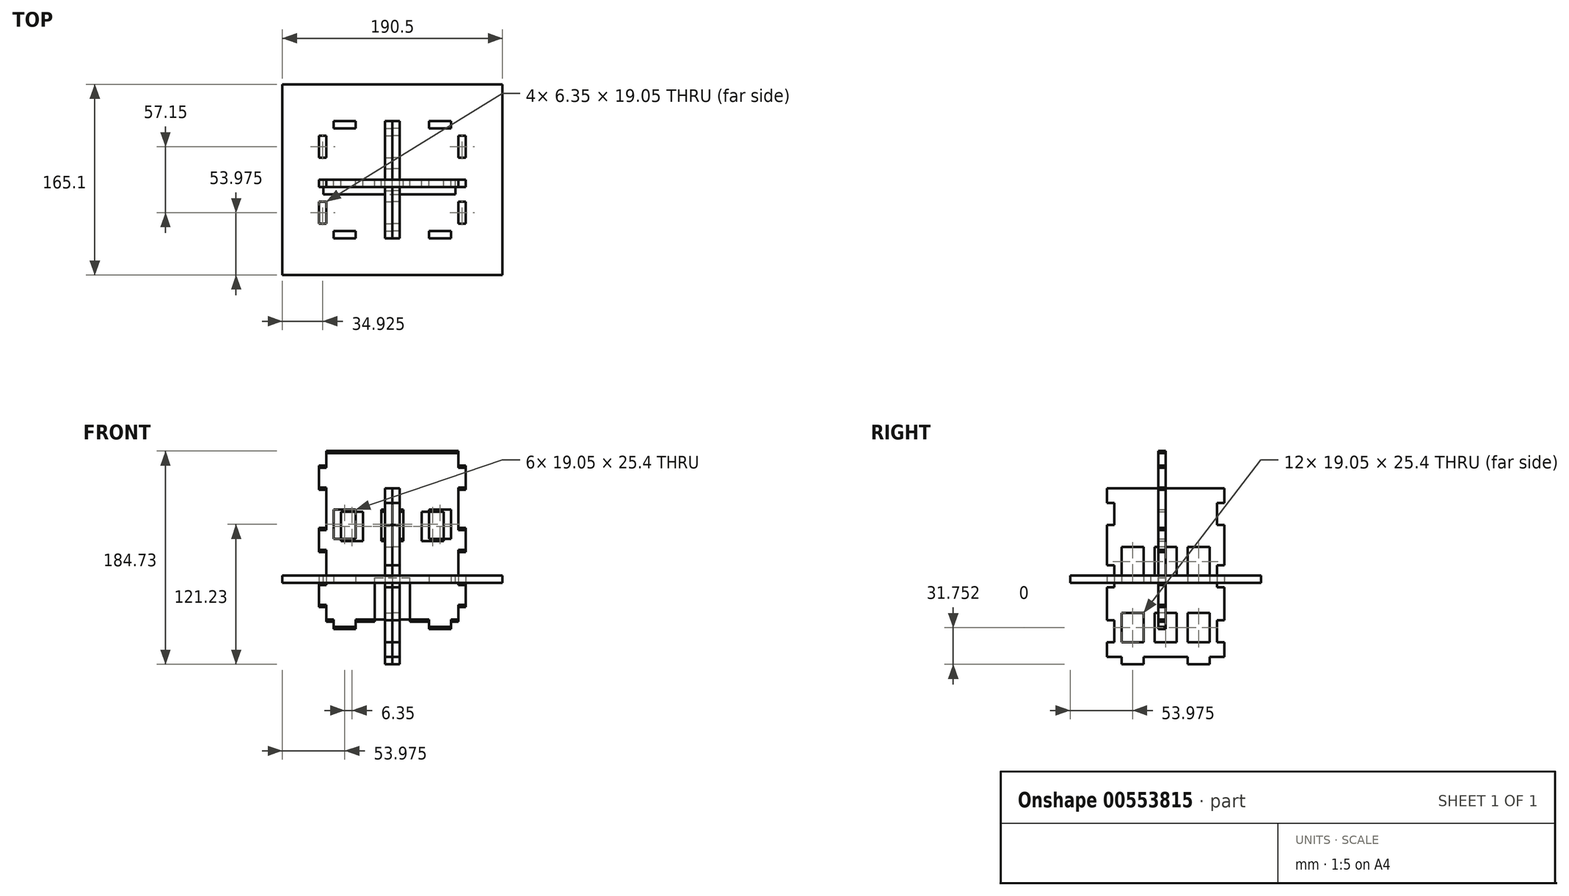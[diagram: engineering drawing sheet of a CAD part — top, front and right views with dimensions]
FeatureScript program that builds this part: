
annotation { "Feature Type Name" : "Feature", "Feature Type Description" : "" }
export const myFeature = defineFeature(function(context is Context, id is Id, definition is map)
    precondition{}
    {
        {
            var Q0;
            Q0=qCreatedBy(makeId("Top.planeOp"),FACE);
            var sketch = newSketch(context, id + "F0", { "sketchPlane" : qUnion([Q0])});
            skLineSegment(sketch, "E0.bottom", {"start": v(63.5, 50.8) * mm, "end": v(-63.5, 50.8) * mm});
            skLineSegment(sketch, "E0.top", {"start": v(63.5, -50.8) * mm, "end": v(-63.5, -50.8) * mm});
            skLineSegment(sketch, "E0.left", {"start": v(63.5, 50.8) * mm, "end": v(63.5, -50.8) * mm});
            skLineSegment(sketch, "E0.right", {"start": v(-63.5, 50.8) * mm, "end": v(-63.5, -50.8) * mm});
            skPoint(sketch, "E0.middle", {"position": v(0, 0) * mm});
            skLineSegment(sketch, "E1", {"start": v(-63.5, -44.45) * mm, "end": v(63.5, -44.45) * mm});
            skLineSegment(sketch, "E2", {"start": v(-50.8, -44.45) * mm, "end": v(-50.8, -50.8) * mm});
            skLineSegment(sketch, "E3", {"start": v(-31.75, -44.45) * mm, "end": v(-31.75, -50.8) * mm});
            skLineSegment(sketch, "E4", {"start": v(50.8, -44.45) * mm, "end": v(50.8, -50.8) * mm});
            skLineSegment(sketch, "E5", {"start": v(31.75, -44.45) * mm, "end": v(31.75, -50.8) * mm});
            skLineSegment(sketch, "E6.MirrorCS", {"start": v(-63.5, 44.45) * mm, "end": v(63.5, 44.45) * mm});
            skLineSegment(sketch, "E7.MirrorCS", {"start": v(50.8, 44.45) * mm, "end": v(50.8, 50.8) * mm});
            skLineSegment(sketch, "E8.MirrorCS", {"start": v(31.75, 44.45) * mm, "end": v(31.75, 50.8) * mm});
            skLineSegment(sketch, "E9.MirrorCS", {"start": v(-50.8, 44.45) * mm, "end": v(-50.8, 50.8) * mm});
            skLineSegment(sketch, "E10.MirrorCS", {"start": v(-31.75, 44.45) * mm, "end": v(-31.75, 50.8) * mm});
            skLineSegment(sketch, "E11", {"start": v(57.15, -44.45) * mm, "end": v(57.15, 44.45) * mm});
            skLineSegment(sketch, "E12", {"start": v(57.15, -38.1) * mm, "end": v(63.5, -38.1) * mm});
            skLineSegment(sketch, "E13", {"start": v(57.15, -19.05) * mm, "end": v(63.5, -19.05) * mm});
            skLineSegment(sketch, "E14", {"start": v(57.15, 19.05) * mm, "end": v(63.5, 19.05) * mm});
            skLineSegment(sketch, "E15", {"start": v(57.15, 38.1) * mm, "end": v(63.5, 38.1) * mm});
            skLineSegment(sketch, "E16.MirrorCS", {"start": v(-57.15, -44.45) * mm, "end": v(-57.15, 44.45) * mm});
            skLineSegment(sketch, "E17.MirrorCS", {"start": v(-57.15, 19.05) * mm, "end": v(-63.5, 19.05) * mm});
            skLineSegment(sketch, "E18.MirrorCS", {"start": v(-57.15, 38.1) * mm, "end": v(-63.5, 38.1) * mm});
            skLineSegment(sketch, "E19.MirrorCS", {"start": v(-57.15, -19.05) * mm, "end": v(-63.5, -19.05) * mm});
            skLineSegment(sketch, "E20.MirrorCS", {"start": v(-57.15, -38.1) * mm, "end": v(-63.5, -38.1) * mm});
            skLineSegment(sketch, "E21.bottom", {"start": v(95.25, -82.55) * mm, "end": v(-95.25, -82.55) * mm});
            skLineSegment(sketch, "E21.top", {"start": v(95.25, 82.55) * mm, "end": v(-95.25, 82.55) * mm});
            skLineSegment(sketch, "E21.left", {"start": v(95.25, -82.55) * mm, "end": v(95.25, 82.55) * mm});
            skLineSegment(sketch, "E21.right", {"start": v(-95.25, -82.55) * mm, "end": v(-95.25, 82.55) * mm});
            skSolve(sketch);
        }
        {
            var Q0;
            {var subQ3=sQuery(id+"F0.wireOp",EDGE,"E7.MirrorCS");Q0=makeQuery(id+"F0.imprint","IMPRINT",FACE,{"disambiguationData":[TD([[makeQuery(id+"F0.imprint","IMPRINT",EDGE,{"derivedFrom":subQ3}),-1.0]])]});}
            var Q1;
            {var subQ3=sQuery(id+"F0.wireOp",EDGE,"E9.MirrorCS");Q1=makeQuery(id+"F0.imprint","IMPRINT",FACE,{"disambiguationData":[TD([[makeQuery(id+"F0.imprint","IMPRINT",EDGE,{"derivedFrom":subQ3}),1.0]])]});}
            var Q2;
            {var subQ0=sQuery(id+"F0.wireOp",EDGE,"E8.MirrorCS");Q2=makeQuery(id+"F0.imprint","IMPRINT",FACE,{"disambiguationData":[TD([[makeQuery(id+"F0.imprint","IMPRINT",EDGE,{"derivedFrom":subQ0}),1.0]])]});}
            var Q3;
            {var subQ3=sQuery(id+"F0.wireOp",EDGE,"E2");Q3=makeQuery(id+"F0.imprint","IMPRINT",FACE,{"disambiguationData":[TD([[makeQuery(id+"F0.imprint","IMPRINT",EDGE,{"derivedFrom":subQ3}),-1.0]])]});}
            var Q4;
            {var subQ0=sQuery(id+"F0.wireOp",EDGE,"E3");Q4=makeQuery(id+"F0.imprint","IMPRINT",FACE,{"disambiguationData":[TD([[makeQuery(id+"F0.imprint","IMPRINT",EDGE,{"derivedFrom":subQ0}),1.0]])]});}
            var Q5;
            {var subQ3=sQuery(id+"F0.wireOp",EDGE,"E4");Q5=makeQuery(id+"F0.imprint","IMPRINT",FACE,{"disambiguationData":[TD([[makeQuery(id+"F0.imprint","IMPRINT",EDGE,{"derivedFrom":subQ3}),1.0]])]});}
            var Q6;
            {var subQ3=sQuery(id+"F0.wireOp",EDGE,"E1");var subQ4=sQuery(id+"F0.wireOp",EDGE,"E0.left");var subQ5=makeQuery(id+"F0.imprint","INTERSECT",VERTEX,{"derivedFrom":[subQ4,subQ3]});Q6=makeQuery(id+"F0.imprint","IMPRINT",FACE,{"disambiguationData":[TD([[makeQuery(id+"F0.imprint","IMPRINT",EDGE,{"disambiguationData":[TD([[subQ5,1.0]])],"derivedFrom":subQ4}),-1.0]])]});}
            var Q7;
            {var subQ4=sQuery(id+"F0.wireOp",EDGE,"E1");var subQ11=makeQuery(id+"F0.imprint","INTERSECT",VERTEX,{"derivedFrom":[subQ4,sQuery(id+"F0.wireOp",EDGE,"E2")]});Q7=makeQuery(id+"F0.imprint","IMPRINT",FACE,{"disambiguationData":[TD([[makeQuery(id+"F0.imprint","IMPRINT",EDGE,{"disambiguationData":[TD([[subQ11,1.0]])],"derivedFrom":subQ4}),1.0]])]});}
            var Q8;
            {var subQ0=sQuery(id+"F0.wireOp",EDGE,"E13");Q8=makeQuery(id+"F0.imprint","IMPRINT",FACE,{"disambiguationData":[TD([[makeQuery(id+"F0.imprint","IMPRINT",EDGE,{"derivedFrom":subQ0}),1.0]])]});}
            var Q9;
            {var subQ3=sQuery(id+"F0.wireOp",EDGE,"E15");Q9=makeQuery(id+"F0.imprint","IMPRINT",FACE,{"disambiguationData":[TD([[makeQuery(id+"F0.imprint","IMPRINT",EDGE,{"derivedFrom":subQ3}),1.0]])]});}
            var Q10;
            {var subQ3=sQuery(id+"F0.wireOp",EDGE,"E20.MirrorCS");Q10=makeQuery(id+"F0.imprint","IMPRINT",FACE,{"disambiguationData":[TD([[makeQuery(id+"F0.imprint","IMPRINT",EDGE,{"derivedFrom":subQ3}),1.0]])]});}
            var Q11;
            {var subQ3=sQuery(id+"F0.wireOp",EDGE,"E18.MirrorCS");Q11=makeQuery(id+"F0.imprint","IMPRINT",FACE,{"disambiguationData":[TD([[makeQuery(id+"F0.imprint","IMPRINT",EDGE,{"derivedFrom":subQ3}),-1.0]])]});}
            var Q12;
            {var subQ0=sQuery(id+"F0.wireOp",EDGE,"E17.MirrorCS");Q12=makeQuery(id+"F0.imprint","IMPRINT",FACE,{"disambiguationData":[TD([[makeQuery(id+"F0.imprint","IMPRINT",EDGE,{"derivedFrom":subQ0}),1.0]])]});}
            var Q13;
            Q13=makeQuery(id+"F0.imprint","IMPRINT",FACE,{"disambiguationData":[TD([[makeQuery(id+"F0.imprint","IMPRINT",EDGE,{"derivedFrom":sQuery(id+"F0.wireOp",EDGE,"E21.bottom")}),-1.0]])]});
            extrude(context, id + "F1", {"entities" : qUnion([Q0, Q1, Q2, Q3, Q4, Q5, Q6, Q7, Q8, Q9, Q10, Q11, Q12, Q13]), "depth" : 6.35 * mm, "offsetDistance" : 25.4 * mm});
        }
        {
            var Q0;
            Q0=qCreatedBy(makeId("Front.planeOp"),FACE);
            var sketch = newSketch(context, id + "F2", { "sketchPlane" : qUnion([Q0])});
            skLineSegment(sketch, "E22.bottom", {"start": v(-63.5, 112.4) * mm, "end": v(63.5, 112.4) * mm});
            skLineSegment(sketch, "E22.top", {"start": v(-63.5, -40) * mm, "end": v(63.5, -40) * mm});
            skLineSegment(sketch, "E22.left", {"start": v(-63.5, 112.4) * mm, "end": v(-63.5, -40) * mm});
            skLineSegment(sketch, "E22.right", {"start": v(63.5, 112.4) * mm, "end": v(63.5, -40) * mm});
            skPoint(sketch, "E22.middle", {"position": v(0, 36.2) * mm});
            skLineSegment(sketch, "E23", {"start": v(-63.5, -33.66) * mm, "end": v(63.5, -33.66) * mm});
            skLineSegment(sketch, "E24", {"start": v(-50.8, -33.66) * mm, "end": v(-50.8, -40) * mm});
            skLineSegment(sketch, "E25", {"start": v(50.8, -40) * mm, "end": v(50.8, -33.66) * mm});
            skLineSegment(sketch, "E26", {"start": v(-31.75, -40) * mm, "end": v(-31.75, -33.66) * mm});
            skLineSegment(sketch, "E27", {"start": v(31.75, -40) * mm, "end": v(31.75, -33.66) * mm});
            skLineSegment(sketch, "E28.bottom", {"start": v(-15.24, -33.66) * mm, "end": v(15.24, -33.66) * mm});
            skLineSegment(sketch, "E28.top", {"start": v(-15.24, 4.45) * mm, "end": v(15.24, 4.45) * mm});
            skLineSegment(sketch, "E28.left", {"start": v(-15.24, -33.66) * mm, "end": v(-15.24, 4.45) * mm});
            skLineSegment(sketch, "E28.right", {"start": v(15.24, -33.66) * mm, "end": v(15.24, 4.45) * mm});
            skLineSegment(sketch, "E29", {"start": v(-63.5, 17.14) * mm, "end": v(63.5, 17.14) * mm, "construction": true});
            skLineSegment(sketch, "E30", {"start": v(-63.5, 23.5) * mm, "end": v(63.5, 23.5) * mm, "construction": true});
            skLineSegment(sketch, "E31", {"start": v(-63.5, 36.2) * mm, "end": v(63.5, 36.2) * mm, "construction": true});
            skLineSegment(sketch, "E32.bottom", {"start": v(-44.45, 36.2) * mm, "end": v(-25.4, 36.2) * mm});
            skLineSegment(sketch, "E32.top", {"start": v(-44.45, 61.6) * mm, "end": v(-25.4, 61.6) * mm});
            skLineSegment(sketch, "E32.left", {"start": v(-44.45, 36.2) * mm, "end": v(-44.45, 61.6) * mm});
            skLineSegment(sketch, "E32.right", {"start": v(-25.4, 36.2) * mm, "end": v(-25.4, 61.6) * mm});
            skLineSegment(sketch, "E33.bottom", {"start": v(25.4, 36.2) * mm, "end": v(44.45, 36.2) * mm});
            skLineSegment(sketch, "E33.top", {"start": v(25.4, 61.6) * mm, "end": v(44.45, 61.6) * mm});
            skLineSegment(sketch, "E33.left", {"start": v(25.4, 36.2) * mm, "end": v(25.4, 61.6) * mm});
            skLineSegment(sketch, "E33.right", {"start": v(44.45, 36.2) * mm, "end": v(44.45, 61.6) * mm});
            skLineSegment(sketch, "E34.bottom", {"start": v(-9.52, 36.2) * mm, "end": v(9.53, 36.2) * mm});
            skLineSegment(sketch, "E34.top", {"start": v(-9.52, 61.6) * mm, "end": v(9.53, 61.6) * mm});
            skLineSegment(sketch, "E34.left", {"start": v(-9.52, 36.2) * mm, "end": v(-9.52, 61.6) * mm});
            skLineSegment(sketch, "E34.right", {"start": v(9.53, 36.2) * mm, "end": v(9.53, 61.6) * mm});
            skLineSegment(sketch, "E35", {"start": v(-63.5, 87) * mm, "end": v(63.5, 87) * mm, "construction": true});
            skLineSegment(sketch, "E36.bottom", {"start": v(-63.5, 80.64) * mm, "end": v(-57.15, 80.64) * mm});
            skLineSegment(sketch, "E36.top", {"start": v(-63.5, 45.72) * mm, "end": v(-57.15, 45.72) * mm});
            skLineSegment(sketch, "E36.left", {"start": v(-63.5, 80.64) * mm, "end": v(-63.5, 45.72) * mm});
            skLineSegment(sketch, "E36.right", {"start": v(-57.15, 80.64) * mm, "end": v(-57.15, 45.72) * mm});
            skLineSegment(sketch, "E37.bottom", {"start": v(-63.5, 26.67) * mm, "end": v(-57.15, 26.67) * mm});
            skLineSegment(sketch, "E37.top", {"start": v(-63.5, -1.9) * mm, "end": v(-57.15, -1.9) * mm});
            skLineSegment(sketch, "E37.left", {"start": v(-63.5, 26.67) * mm, "end": v(-63.5, -1.9) * mm});
            skLineSegment(sketch, "E37.right", {"start": v(-57.15, 26.67) * mm, "end": v(-57.15, -1.9) * mm});
            skLineSegment(sketch, "E38.MirrorCS", {"start": v(57.15, 80.64) * mm, "end": v(57.15, 45.72) * mm});
            skLineSegment(sketch, "E39.MirrorCS", {"start": v(63.5, 80.64) * mm, "end": v(57.15, 80.64) * mm});
            skLineSegment(sketch, "E40.MirrorCS", {"start": v(63.5, 45.72) * mm, "end": v(57.15, 45.72) * mm});
            skLineSegment(sketch, "E41.MirrorCS", {"start": v(63.5, 26.67) * mm, "end": v(57.15, 26.67) * mm});
            skLineSegment(sketch, "E42.MirrorCS", {"start": v(57.15, 26.67) * mm, "end": v(57.15, -1.9) * mm});
            skLineSegment(sketch, "E43.MirrorCS", {"start": v(63.5, -1.9) * mm, "end": v(57.15, -1.9) * mm});
            skLineSegment(sketch, "E44.bottom", {"start": v(-63.5, 112.4) * mm, "end": v(-57.15, 112.4) * mm});
            skLineSegment(sketch, "E44.top", {"start": v(-63.5, 99.7) * mm, "end": v(-57.15, 99.7) * mm});
            skLineSegment(sketch, "E44.left", {"start": v(-63.5, 112.4) * mm, "end": v(-63.5, 99.7) * mm});
            skLineSegment(sketch, "E44.right", {"start": v(-57.15, 112.4) * mm, "end": v(-57.15, 99.7) * mm});
            skLineSegment(sketch, "E45.MirrorCS", {"start": v(57.15, 112.4) * mm, "end": v(57.15, 99.7) * mm});
            skLineSegment(sketch, "E46.MirrorCS", {"start": v(63.5, 99.7) * mm, "end": v(57.15, 99.7) * mm});
            skLineSegment(sketch, "E47.bottom", {"start": v(-63.5, -33.66) * mm, "end": v(-57.15, -33.66) * mm});
            skLineSegment(sketch, "E47.top", {"start": v(-63.5, -20.96) * mm, "end": v(-57.15, -20.96) * mm});
            skLineSegment(sketch, "E47.left", {"start": v(-63.5, -33.66) * mm, "end": v(-63.5, -20.96) * mm});
            skLineSegment(sketch, "E47.right", {"start": v(-57.15, -33.66) * mm, "end": v(-57.15, -20.96) * mm});
            skLineSegment(sketch, "E48.MirrorCS", {"start": v(57.15, -33.66) * mm, "end": v(57.15, -20.96) * mm});
            skLineSegment(sketch, "E49.MirrorCS", {"start": v(63.5, -20.96) * mm, "end": v(57.15, -20.96) * mm});
            skSolve(sketch);
        }
        {
            var Q0;
            Q0=makeQuery(id+"F2.imprint","IMPRINT",FACE,{"disambiguationData":[TD([[makeQuery(id+"F2.imprint","IMPRINT",EDGE,{"derivedFrom":sQuery(id+"F2.wireOp",EDGE,"E28.top")}),1.0]])]});
            var Q1;
            {var subQ0=sQuery(id+"F2.wireOp",EDGE,"E25");Q1=makeQuery(id+"F2.imprint","IMPRINT",FACE,{"disambiguationData":[TD([[makeQuery(id+"F2.imprint","IMPRINT",EDGE,{"derivedFrom":subQ0}),1.0]])]});}
            var Q2;
            {var subQ0=sQuery(id+"F2.wireOp",EDGE,"E24");Q2=makeQuery(id+"F2.imprint","IMPRINT",FACE,{"disambiguationData":[TD([[makeQuery(id+"F2.imprint","IMPRINT",EDGE,{"derivedFrom":subQ0}),1.0]])]});}
            extrude(context, id + "F3", {"entities" : qUnion([Q0, Q1, Q2]), "depth" : 6.35 * mm, "offsetDistance" : 25.4 * mm});
        }
        {
            var Q0;
            Q0=qCreatedBy(makeId("Front.planeOp"),FACE);
            var sketch = newSketch(context, id + "F4", { "sketchPlane" : qUnion([Q0])});
            skLineSegment(sketch, "E50.bottom", {"start": v(-63.5, 114.3) * mm, "end": v(63.5, 114.3) * mm});
            skLineSegment(sketch, "E50.top", {"start": v(-63.5, -38.1) * mm, "end": v(63.5, -38.1) * mm});
            skLineSegment(sketch, "E50.left", {"start": v(-63.5, 114.3) * mm, "end": v(-63.5, -38.1) * mm});
            skLineSegment(sketch, "E50.right", {"start": v(63.5, 114.3) * mm, "end": v(63.5, -38.1) * mm});
            skPoint(sketch, "E50.middle", {"position": v(0, 38.1) * mm});
            skLineSegment(sketch, "E51", {"start": v(-63.5, -31.75) * mm, "end": v(63.5, -31.75) * mm});
            skLineSegment(sketch, "E52", {"start": v(-50.8, -31.75) * mm, "end": v(-50.8, -38.1) * mm});
            skLineSegment(sketch, "E53", {"start": v(50.8, -38.1) * mm, "end": v(50.8, -31.75) * mm});
            skLineSegment(sketch, "E54", {"start": v(-31.75, -38.1) * mm, "end": v(-31.75, -31.75) * mm});
            skLineSegment(sketch, "E55", {"start": v(31.75, -38.1) * mm, "end": v(31.75, -31.75) * mm});
            skLineSegment(sketch, "E56", {"start": v(63.5, 38.1) * mm, "end": v(-63.5, 38.1) * mm, "construction": true});
            skLineSegment(sketch, "E57.bottom", {"start": v(50.8, 38.1) * mm, "end": v(31.75, 38.1) * mm});
            skLineSegment(sketch, "E57.top", {"start": v(50.8, 63.5) * mm, "end": v(31.75, 63.5) * mm});
            skLineSegment(sketch, "E57.left", {"start": v(50.8, 38.1) * mm, "end": v(50.8, 63.5) * mm});
            skLineSegment(sketch, "E57.right", {"start": v(31.75, 38.1) * mm, "end": v(31.75, 63.5) * mm});
            skLineSegment(sketch, "E58.bottom", {"start": v(-31.75, 38.1) * mm, "end": v(-50.8, 38.1) * mm});
            skLineSegment(sketch, "E58.top", {"start": v(-31.75, 63.5) * mm, "end": v(-50.8, 63.5) * mm});
            skLineSegment(sketch, "E58.left", {"start": v(-31.75, 38.1) * mm, "end": v(-31.75, 63.5) * mm});
            skLineSegment(sketch, "E58.right", {"start": v(-50.8, 38.1) * mm, "end": v(-50.8, 63.5) * mm});
            skLineSegment(sketch, "E59.bottom", {"start": v(9.52, 38.1) * mm, "end": v(-9.53, 38.1) * mm});
            skLineSegment(sketch, "E59.top", {"start": v(9.52, 63.5) * mm, "end": v(-9.53, 63.5) * mm});
            skLineSegment(sketch, "E59.left", {"start": v(9.52, 38.1) * mm, "end": v(9.52, 63.5) * mm});
            skLineSegment(sketch, "E59.right", {"start": v(-9.53, 38.1) * mm, "end": v(-9.53, 63.5) * mm});
            skLineSegment(sketch, "E60.bottom", {"start": v(-63.5, 114.3) * mm, "end": v(-57.15, 114.3) * mm});
            skLineSegment(sketch, "E60.top", {"start": v(-63.5, 101.6) * mm, "end": v(-57.15, 101.6) * mm});
            skLineSegment(sketch, "E60.left", {"start": v(-63.5, 114.3) * mm, "end": v(-63.5, 101.6) * mm});
            skLineSegment(sketch, "E60.right", {"start": v(-57.15, 114.3) * mm, "end": v(-57.15, 101.6) * mm});
            skLineSegment(sketch, "E61.bottom", {"start": v(-63.5, -31.75) * mm, "end": v(-57.15, -31.75) * mm});
            skLineSegment(sketch, "E61.top", {"start": v(-63.5, -19.05) * mm, "end": v(-57.15, -19.05) * mm});
            skLineSegment(sketch, "E61.left", {"start": v(-63.5, -31.75) * mm, "end": v(-63.5, -19.05) * mm});
            skLineSegment(sketch, "E61.right", {"start": v(-57.15, -31.75) * mm, "end": v(-57.15, -19.05) * mm});
            skLineSegment(sketch, "E62.bottom", {"start": v(-63.5, 82.55) * mm, "end": v(-57.15, 82.55) * mm});
            skLineSegment(sketch, "E62.top", {"start": v(-63.5, 47.63) * mm, "end": v(-57.15, 47.63) * mm});
            skLineSegment(sketch, "E62.left", {"start": v(-63.5, 82.55) * mm, "end": v(-63.5, 47.63) * mm});
            skLineSegment(sketch, "E62.right", {"start": v(-57.15, 82.55) * mm, "end": v(-57.15, 47.63) * mm});
            skLineSegment(sketch, "E63.bottom", {"start": v(-63.5, 28.58) * mm, "end": v(-57.15, 28.58) * mm});
            skLineSegment(sketch, "E63.top", {"start": v(-63.5, 0) * mm, "end": v(-57.15, 0) * mm});
            skLineSegment(sketch, "E63.left", {"start": v(-63.5, 28.58) * mm, "end": v(-63.5, 0) * mm});
            skLineSegment(sketch, "E63.right", {"start": v(-57.15, 28.58) * mm, "end": v(-57.15, 0) * mm});
            skLineSegment(sketch, "E64.MirrorCS", {"start": v(57.15, 114.3) * mm, "end": v(57.15, 101.6) * mm});
            skLineSegment(sketch, "E65.MirrorCS", {"start": v(63.5, 101.6) * mm, "end": v(57.15, 101.6) * mm});
            skLineSegment(sketch, "E66.MirrorCS", {"start": v(63.5, 82.55) * mm, "end": v(57.15, 82.55) * mm});
            skLineSegment(sketch, "E67.MirrorCS", {"start": v(63.5, 47.63) * mm, "end": v(57.15, 47.63) * mm});
            skLineSegment(sketch, "E68.MirrorCS", {"start": v(57.15, 82.55) * mm, "end": v(57.15, 47.63) * mm});
            skLineSegment(sketch, "E69.MirrorCS", {"start": v(63.5, 28.58) * mm, "end": v(57.15, 28.58) * mm});
            skLineSegment(sketch, "E70.MirrorCS", {"start": v(63.5, 0) * mm, "end": v(57.15, 0) * mm});
            skLineSegment(sketch, "E71.MirrorCS", {"start": v(57.15, 28.58) * mm, "end": v(57.15, 0) * mm});
            skLineSegment(sketch, "E72.MirrorCS", {"start": v(63.5, -19.05) * mm, "end": v(57.15, -19.05) * mm});
            skLineSegment(sketch, "E73.MirrorCS", {"start": v(57.15, -31.75) * mm, "end": v(57.15, -19.05) * mm});
            skSolve(sketch);
        }
        {
            var Q0;
            {var subQ0=sQuery(id+"F4.wireOp",EDGE,"E52");Q0=makeQuery(id+"F4.imprint","IMPRINT",FACE,{"disambiguationData":[TD([[makeQuery(id+"F4.imprint","IMPRINT",EDGE,{"derivedFrom":subQ0}),1.0]])]});}
            var Q1;
            {var subQ0=sQuery(id+"F4.wireOp",EDGE,"E53");Q1=makeQuery(id+"F4.imprint","IMPRINT",FACE,{"disambiguationData":[TD([[makeQuery(id+"F4.imprint","IMPRINT",EDGE,{"derivedFrom":subQ0}),1.0]])]});}
            var Q2;
            {var subQ0=sQuery(id+"F4.wireOp",EDGE,"E57.bottom");Q2=makeQuery(id+"F4.imprint","IMPRINT",FACE,{"disambiguationData":[TD([[makeQuery(id+"F4.imprint","IMPRINT",EDGE,{"derivedFrom":subQ0}),1.0]])]});}
            extrude(context, id + "F5", {"entities" : qUnion([Q0, Q1, Q2]), "depth" : 6.35 * mm, "offsetDistance" : 25.4 * mm});
        }
        {
            var Q0;
            Q0=qCreatedBy(makeId("Front.planeOp"),FACE);
            var sketch = newSketch(context, id + "F6", { "sketchPlane" : qUnion([Q0])});
            skLineSegment(sketch, "E74.bottom", {"start": v(-59.84, 0.21) * mm, "end": v(54.46, 0.21) * mm});
            skLineSegment(sketch, "E74.top", {"start": v(-59.84, 6.56) * mm, "end": v(54.46, 6.56) * mm});
            skLineSegment(sketch, "E74.left", {"start": v(-59.84, 0.21) * mm, "end": v(-59.84, 6.56) * mm});
            skLineSegment(sketch, "E74.right", {"start": v(54.46, 0.21) * mm, "end": v(54.46, 6.56) * mm});
            skSolve(sketch);
        }
        {
            var Q0;
            Q0=makeQuery(id+"F6.imprint","IMPRINT",FACE,{"disambiguationData":[TD([[makeQuery(id+"F6.imprint","IMPRINT",EDGE,{"derivedFrom":sQuery(id+"F6.wireOp",EDGE,"E74.bottom")}),1.0]])]});
            extrude(context, id + "F7", {"entities" : qUnion([Q0]), "depth" : 12.7 * mm, "offsetDistance" : 25.4 * mm});
        }
        {
            var Q0;
            Q0=qCreatedBy(makeId("Right.planeOp"),FACE);
            var sketch = newSketch(context, id + "F8", { "sketchPlane" : qUnion([Q0])});
            skLineSegment(sketch, "E75.bottom", {"start": v(-50.8, 81.97) * mm, "end": v(50.8, 81.97) * mm});
            skLineSegment(sketch, "E75.top", {"start": v(-50.8, -70.43) * mm, "end": v(50.8, -70.43) * mm});
            skLineSegment(sketch, "E75.left", {"start": v(-50.8, 81.97) * mm, "end": v(-50.8, -70.43) * mm});
            skLineSegment(sketch, "E75.right", {"start": v(50.8, 81.97) * mm, "end": v(50.8, -70.43) * mm});
            skPoint(sketch, "E75.middle", {"position": v(0, 5.77) * mm});
            skLineSegment(sketch, "E76", {"start": v(-50.8, -64.08) * mm, "end": v(50.8, -64.08) * mm});
            skLineSegment(sketch, "E77", {"start": v(-38.1, -64.08) * mm, "end": v(-38.1, -70.43) * mm});
            skLineSegment(sketch, "E78", {"start": v(38.1, -70.43) * mm, "end": v(38.1, -64.08) * mm});
            skLineSegment(sketch, "E79", {"start": v(-19.05, -70.43) * mm, "end": v(-19.05, -64.08) * mm});
            skLineSegment(sketch, "E80", {"start": v(19.05, -70.43) * mm, "end": v(19.05, -64.08) * mm});
            skLineSegment(sketch, "E81.bottom", {"start": v(38.1, 5.77) * mm, "end": v(19.05, 5.77) * mm});
            skLineSegment(sketch, "E81.top", {"start": v(38.1, 31.17) * mm, "end": v(19.05, 31.17) * mm});
            skLineSegment(sketch, "E81.left", {"start": v(38.1, 5.77) * mm, "end": v(38.1, 31.17) * mm});
            skLineSegment(sketch, "E81.right", {"start": v(19.05, 5.77) * mm, "end": v(19.05, 31.17) * mm});
            skLineSegment(sketch, "E82.bottom", {"start": v(-19.05, 5.77) * mm, "end": v(-38.1, 5.77) * mm});
            skLineSegment(sketch, "E82.top", {"start": v(-19.05, 31.17) * mm, "end": v(-38.1, 31.17) * mm});
            skLineSegment(sketch, "E82.left", {"start": v(-19.05, 5.77) * mm, "end": v(-19.05, 31.17) * mm});
            skLineSegment(sketch, "E82.right", {"start": v(-38.1, 5.77) * mm, "end": v(-38.1, 31.17) * mm});
            skLineSegment(sketch, "E83.bottom", {"start": v(9.52, 5.77) * mm, "end": v(-9.53, 5.77) * mm});
            skLineSegment(sketch, "E83.top", {"start": v(9.52, 31.17) * mm, "end": v(-9.53, 31.17) * mm});
            skLineSegment(sketch, "E83.left", {"start": v(9.52, 5.77) * mm, "end": v(9.52, 31.17) * mm});
            skLineSegment(sketch, "E83.right", {"start": v(-9.53, 5.77) * mm, "end": v(-9.53, 31.17) * mm});
            skLineSegment(sketch, "E84.bottom", {"start": v(38.1, -51.38) * mm, "end": v(19.05, -51.38) * mm});
            skLineSegment(sketch, "E84.top", {"start": v(38.1, -25.98) * mm, "end": v(19.05, -25.98) * mm});
            skLineSegment(sketch, "E84.left", {"start": v(38.1, -51.38) * mm, "end": v(38.1, -25.98) * mm});
            skLineSegment(sketch, "E84.right", {"start": v(19.05, -51.38) * mm, "end": v(19.05, -25.98) * mm});
            skLineSegment(sketch, "E85.bottom", {"start": v(9.53, -51.38) * mm, "end": v(-9.52, -51.38) * mm});
            skLineSegment(sketch, "E85.top", {"start": v(9.53, -25.98) * mm, "end": v(-9.52, -25.98) * mm});
            skLineSegment(sketch, "E85.left", {"start": v(9.53, -51.38) * mm, "end": v(9.53, -25.98) * mm});
            skLineSegment(sketch, "E85.right", {"start": v(-9.52, -51.38) * mm, "end": v(-9.52, -25.98) * mm});
            skLineSegment(sketch, "E86.bottom", {"start": v(-19.05, -51.38) * mm, "end": v(-38.1, -51.38) * mm});
            skLineSegment(sketch, "E86.top", {"start": v(-19.05, -25.98) * mm, "end": v(-38.1, -25.98) * mm});
            skLineSegment(sketch, "E86.left", {"start": v(-19.05, -51.38) * mm, "end": v(-19.05, -25.98) * mm});
            skLineSegment(sketch, "E86.right", {"start": v(-38.1, -51.38) * mm, "end": v(-38.1, -25.98) * mm});
            skLineSegment(sketch, "E87", {"start": v(-44.45, 81.97) * mm, "end": v(-44.45, -64.08) * mm});
            skLineSegment(sketch, "E88", {"start": v(44.45, 81.97) * mm, "end": v(44.45, -64.08) * mm});
            skLineSegment(sketch, "E89", {"start": v(50.8, 69.27) * mm, "end": v(44.45, 69.27) * mm});
            skLineSegment(sketch, "E90", {"start": v(50.8, 50.22) * mm, "end": v(44.45, 50.22) * mm});
            skLineSegment(sketch, "E91", {"start": v(50.8, 15.3) * mm, "end": v(44.45, 15.3) * mm});
            skLineSegment(sketch, "E92", {"start": v(50.8, -3.75) * mm, "end": v(44.45, -3.75) * mm});
            skLineSegment(sketch, "E93", {"start": v(50.8, -51.38) * mm, "end": v(44.45, -51.38) * mm});
            skLineSegment(sketch, "E94", {"start": v(50.8, -32.33) * mm, "end": v(44.45, -32.33) * mm});
            skLineSegment(sketch, "E95.MirrorCS", {"start": v(-50.8, 50.22) * mm, "end": v(-44.45, 50.22) * mm});
            skLineSegment(sketch, "E96.MirrorCS", {"start": v(-50.8, 69.27) * mm, "end": v(-44.45, 69.27) * mm});
            skLineSegment(sketch, "E97.MirrorCS", {"start": v(-50.8, 15.3) * mm, "end": v(-44.45, 15.3) * mm});
            skLineSegment(sketch, "E98.MirrorCS", {"start": v(-50.8, -3.75) * mm, "end": v(-44.45, -3.75) * mm});
            skLineSegment(sketch, "E99.MirrorCS", {"start": v(-50.8, -32.33) * mm, "end": v(-44.45, -32.33) * mm});
            skLineSegment(sketch, "E100.MirrorCS", {"start": v(-50.8, -51.38) * mm, "end": v(-44.45, -51.38) * mm});
            skSolve(sketch);
        }
        {
            var Q0;
            {var subQ0=sQuery(id+"F8.wireOp",EDGE,"E77");Q0=makeQuery(id+"F8.imprint","IMPRINT",FACE,{"disambiguationData":[TD([[makeQuery(id+"F8.imprint","IMPRINT",EDGE,{"derivedFrom":subQ0}),1.0]])]});}
            var Q1;
            {var subQ0=sQuery(id+"F8.wireOp",EDGE,"E78");Q1=makeQuery(id+"F8.imprint","IMPRINT",FACE,{"disambiguationData":[TD([[makeQuery(id+"F8.imprint","IMPRINT",EDGE,{"derivedFrom":subQ0}),1.0]])]});}
            var Q2;
            {var subQ3=sQuery(id+"F8.wireOp",EDGE,"E75.bottom");Q2=makeQuery(id+"F8.imprint","IMPRINT",FACE,{"disambiguationData":[TD([[makeQuery(id+"F8.imprint","IMPRINT",EDGE,{"derivedFrom":subQ3}),-1.0]])]});}
            var Q3;
            {var subQ7=sQuery(id+"F8.wireOp",EDGE,"E81.bottom");Q3=makeQuery(id+"F8.imprint","IMPRINT",FACE,{"disambiguationData":[TD([[makeQuery(id+"F8.imprint","IMPRINT",EDGE,{"derivedFrom":subQ7}),1.0]])]});}
            var Q4;
            {var subQ0=sQuery(id+"F8.wireOp",EDGE,"E84.bottom");Q4=makeQuery(id+"F8.imprint","IMPRINT",FACE,{"disambiguationData":[TD([[makeQuery(id+"F8.imprint","IMPRINT",EDGE,{"derivedFrom":subQ0}),1.0]])]});}
            var Q5;
            {var subQ0=sQuery(id+"F8.wireOp",EDGE,"E92");Q5=makeQuery(id+"F8.imprint","IMPRINT",FACE,{"disambiguationData":[TD([[makeQuery(id+"F8.imprint","IMPRINT",EDGE,{"derivedFrom":subQ0}),1.0]])]});}
            var Q6;
            {var subQ3=sQuery(id+"F8.wireOp",EDGE,"E93");Q6=makeQuery(id+"F8.imprint","IMPRINT",FACE,{"disambiguationData":[TD([[makeQuery(id+"F8.imprint","IMPRINT",EDGE,{"derivedFrom":subQ3}),1.0]])]});}
            var Q7;
            {var subQ0=sQuery(id+"F8.wireOp",EDGE,"E90");Q7=makeQuery(id+"F8.imprint","IMPRINT",FACE,{"disambiguationData":[TD([[makeQuery(id+"F8.imprint","IMPRINT",EDGE,{"derivedFrom":subQ0}),1.0]])]});}
            var Q8;
            {var subQ3=sQuery(id+"F8.wireOp",EDGE,"E100.MirrorCS");Q8=makeQuery(id+"F8.imprint","IMPRINT",FACE,{"disambiguationData":[TD([[makeQuery(id+"F8.imprint","IMPRINT",EDGE,{"derivedFrom":subQ3}),-1.0]])]});}
            var Q9;
            {var subQ0=sQuery(id+"F8.wireOp",EDGE,"E98.MirrorCS");Q9=makeQuery(id+"F8.imprint","IMPRINT",FACE,{"disambiguationData":[TD([[makeQuery(id+"F8.imprint","IMPRINT",EDGE,{"derivedFrom":subQ0}),-1.0]])]});}
            var Q10;
            {var subQ0=sQuery(id+"F8.wireOp",EDGE,"E95.MirrorCS");Q10=makeQuery(id+"F8.imprint","IMPRINT",FACE,{"disambiguationData":[TD([[makeQuery(id+"F8.imprint","IMPRINT",EDGE,{"derivedFrom":subQ0}),-1.0]])]});}
            extrude(context, id + "F9", {"entities" : qUnion([Q0, Q1, Q2, Q3, Q4, Q5, Q6, Q7, Q8, Q9, Q10]), "depth" : 6.35 * mm, "offsetDistance" : 25.4 * mm});
        }
        {
            var Q0;
            Q0=makeQuery(id+"F9.opExtrude","SWEPT_BODY",BODY,{"disambiguationData":[OSD([sQuery(id+"F8.wireOp",EDGE,"E75.bottom"),sQuery(id+"F8.wireOp",EDGE,"E75.top"),sQuery(id+"F8.wireOp",EDGE,"E75.left"),sQuery(id+"F8.wireOp",EDGE,"E75.right"),sQuery(id+"F8.wireOp",EDGE,"E76"),sQuery(id+"F8.wireOp",EDGE,"E77"),sQuery(id+"F8.wireOp",EDGE,"E78"),sQuery(id+"F8.wireOp",EDGE,"E79"),sQuery(id+"F8.wireOp",EDGE,"E80"),sQuery(id+"F8.wireOp",EDGE,"E81.bottom"),sQuery(id+"F8.wireOp",EDGE,"E81.top"),sQuery(id+"F8.wireOp",EDGE,"E81.left"),sQuery(id+"F8.wireOp",EDGE,"E81.right"),sQuery(id+"F8.wireOp",EDGE,"E82.bottom"),sQuery(id+"F8.wireOp",EDGE,"E82.top"),sQuery(id+"F8.wireOp",EDGE,"E82.left"),sQuery(id+"F8.wireOp",EDGE,"E82.right"),sQuery(id+"F8.wireOp",EDGE,"E83.bottom"),sQuery(id+"F8.wireOp",EDGE,"E83.top"),sQuery(id+"F8.wireOp",EDGE,"E83.left"),sQuery(id+"F8.wireOp",EDGE,"E83.right"),sQuery(id+"F8.wireOp",EDGE,"E84.bottom"),sQuery(id+"F8.wireOp",EDGE,"E84.top"),sQuery(id+"F8.wireOp",EDGE,"E84.left"),sQuery(id+"F8.wireOp",EDGE,"E84.right"),sQuery(id+"F8.wireOp",EDGE,"E85.bottom"),sQuery(id+"F8.wireOp",EDGE,"E85.top"),sQuery(id+"F8.wireOp",EDGE,"E85.left"),sQuery(id+"F8.wireOp",EDGE,"E85.right"),sQuery(id+"F8.wireOp",EDGE,"E86.bottom"),sQuery(id+"F8.wireOp",EDGE,"E86.top"),sQuery(id+"F8.wireOp",EDGE,"E86.left"),sQuery(id+"F8.wireOp",EDGE,"E86.right")])]});
            var Q1;
            Q1=qCreatedBy(makeId("Right.planeOp"),FACE);
            mirror(context, id + "F10", {"entities" : qUnion([Q0]), "mirrorPlane" : qUnion([Q1])});
        }
    });
